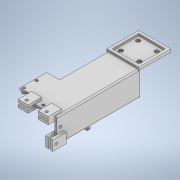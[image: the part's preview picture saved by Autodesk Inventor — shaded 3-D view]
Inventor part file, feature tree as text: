
AUTODESK INVENTOR PART (.ipt)
format: ipt  version: 2020 (Build 240168000, 168)  size: 425,472 bytes
history: native  units: in
note: dims shown in document units (in); Inventor stores cm internally (conversion verified against a paired STEP export)
features: extrude x20, sketch x20, mirror x3, fillet x1
ambient origin geometry x8: Origin, YZ Plane, XZ Plane, XY Plane, X Axis, Y Axis, Z Axis, Center Point
bodies: Solid1 (feature_tree)
feature tree (44):
  extrude  "Extrusion1"  Depth=1.8898in
  extrude  "Extrusion2"  Depth=0.1575in
  mirror  "Mirror1"
  extrude  "Extrusion3"  Depth=0.1575in
  extrude  "Extrusion4"  Depth=0.1575in
  extrude  "Extrusion5"  Depth=0.1181in
  extrude  "Extrusion6"  Depth=0.1181in
  mirror  "Mirror2"
  extrude  "Extrusion7"  Depth=0.1575in
  mirror  "Mirror3"
  extrude  "Extrusion8"  Depth=0.1575in
  extrude  "Extrusion9"  Depth=0.1575in
  extrude  "Extrusion10"  Depth=0.2362in
  extrude  "Extrusion11"  Depth=0.2362in
  extrude  "Extrusion20"  Depth=0.1575in TaperAngle=0.0deg
  extrude  "Extrusion21"  Depth=1.6654in TaperAngle=0.0deg
  extrude  "Extrusion24"  Depth=0.315in
  extrude  "Extrusion25"  Depth=0.315in
  extrude  "Extrusion26"  Depth=0.2362in
  extrude  "Extrusion27"  Depth=0.2362in
  extrude  "Extrusion28"  Depth=0.0787in TaperAngle=0.0deg
  extrude  "Extrusion29"  Depth=0.1575in
  extrude  "Extrusion30"  Depth=0.1575in
  fillet  "Fillet3"  Radius=0.1575in
  sketch  "Sketch1"  dims[d0=1.8898in d1=10.8661in]
  sketch  "Sketch2"  dims[d2=0.1181in d3=0.0in d4=0.1575in]
  sketch  "Sketch3"  dims[d5=1.8898in d6=0.1575in]
  sketch  "Sketch4"  dims[d7=0.1575in d8=0.1575in]
  sketch  "Sketch5"  dims[d9=0.1181in d10=0.0in d11=0.1181in]
  sketch  "Sketch6"  dims[d12=0.1181in d13=0.1181in]
  sketch  "Sketch7"  dims[d14=1.378in d15=0.0in d16=0.1575in]
  sketch  "Sketch8"  dims[d17=0.315in d18=0.0in d19=0.1575in]
  sketch  "Sketch9"  dims[d20=0.1575in d21=0.0in d22=0.1575in]
  sketch  "Sketch10"  dims[d23=0.1575in d24=0.0in d25=0.2362in]
  sketch  "Sketch11"  dims[d26=0.2362in d27=0.2362in]
  sketch  "Sketch20"  dims[d28=0.2362in d29=0.1575in d30=0.0in]
  sketch  "Sketch21"  dims[d31=0.1181in d32=1.6654in d33=0.0in]
  sketch  "Sketch24"  dims[d34=0.315in d35=0.315in]
  sketch  "Sketch25"  dims[d36=0.315in d37=0.315in]
  sketch  "Sketch26"  dims[d38=0.1181in d39=0.0in d40=0.2362in]
  sketch  "Sketch27"  dims[d41=0.2362in d42=0.2362in]
  sketch  "Sketch28"  dims[d43=0.2362in d44=0.0787in d45=0.0in]
  sketch  "Sketch29"  dims[d46=0.9843in d47=0.1575in]
  sketch  "Sketch30"  dims[d48=0.1575in d49=0.1575in d50=0.1575in d51=0.3937in d52=0.0in d84=3.937in d85=0.0in d86=0.5906in d87=0.7874in d88=0.5906in d89=0.7874in d90=0.1575in d91=0.2756in d92=0.0in d93=0.0in d102=0.1575in d103=0.1575in d104=0.1575in d105=0.5906in d106=0.0in d107=0.7874in d108=0.5906in d109=0.1575in d110=0.2756in d111=0.0in d112=0.0in d115=0.3937in d116=0.0in d117=0.1575in d118=0.1575in d119=0.7874in d120=0.0in d123=1.5748in d124=0.689in d125=0.0in d126=0.2362in d127=0.2362in d128=0.1181in d129=0.0in d130=0.1575in d131=0.1575in d132=0.3937in d133=0.0in d134=0.0787in d135=1.1024in d136=1.0236in d137=1.1024in d138=1.0236in d139=0.2756in d140=0.2756in d141=0.2362in d142=0.2362in]
